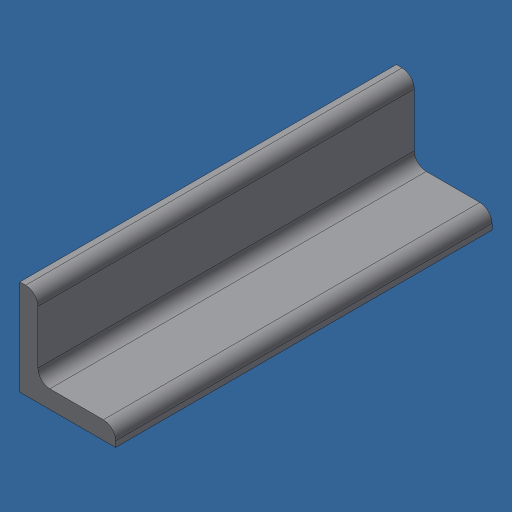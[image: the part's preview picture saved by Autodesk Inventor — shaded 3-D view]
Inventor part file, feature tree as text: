
AUTODESK INVENTOR PART (.ipt)
format: ipt  version: 2024.3 (Build 283343000, 343)  size: 114,688 bytes
history: native  units: mm (DEFAULTED — no unit token found)
features: other x1, extrude x1
ambient origin geometry x8: Origin, YZ Plane, XZ Plane, XY Plane, X Axis, Y Axis, Z Axis, Center Point
bodies: Body1 (feature_tree)
feature tree (2):
  other  "Finish - None"
  extrude  "1" X 1" X 3/16""  Depth=4.7625mm
